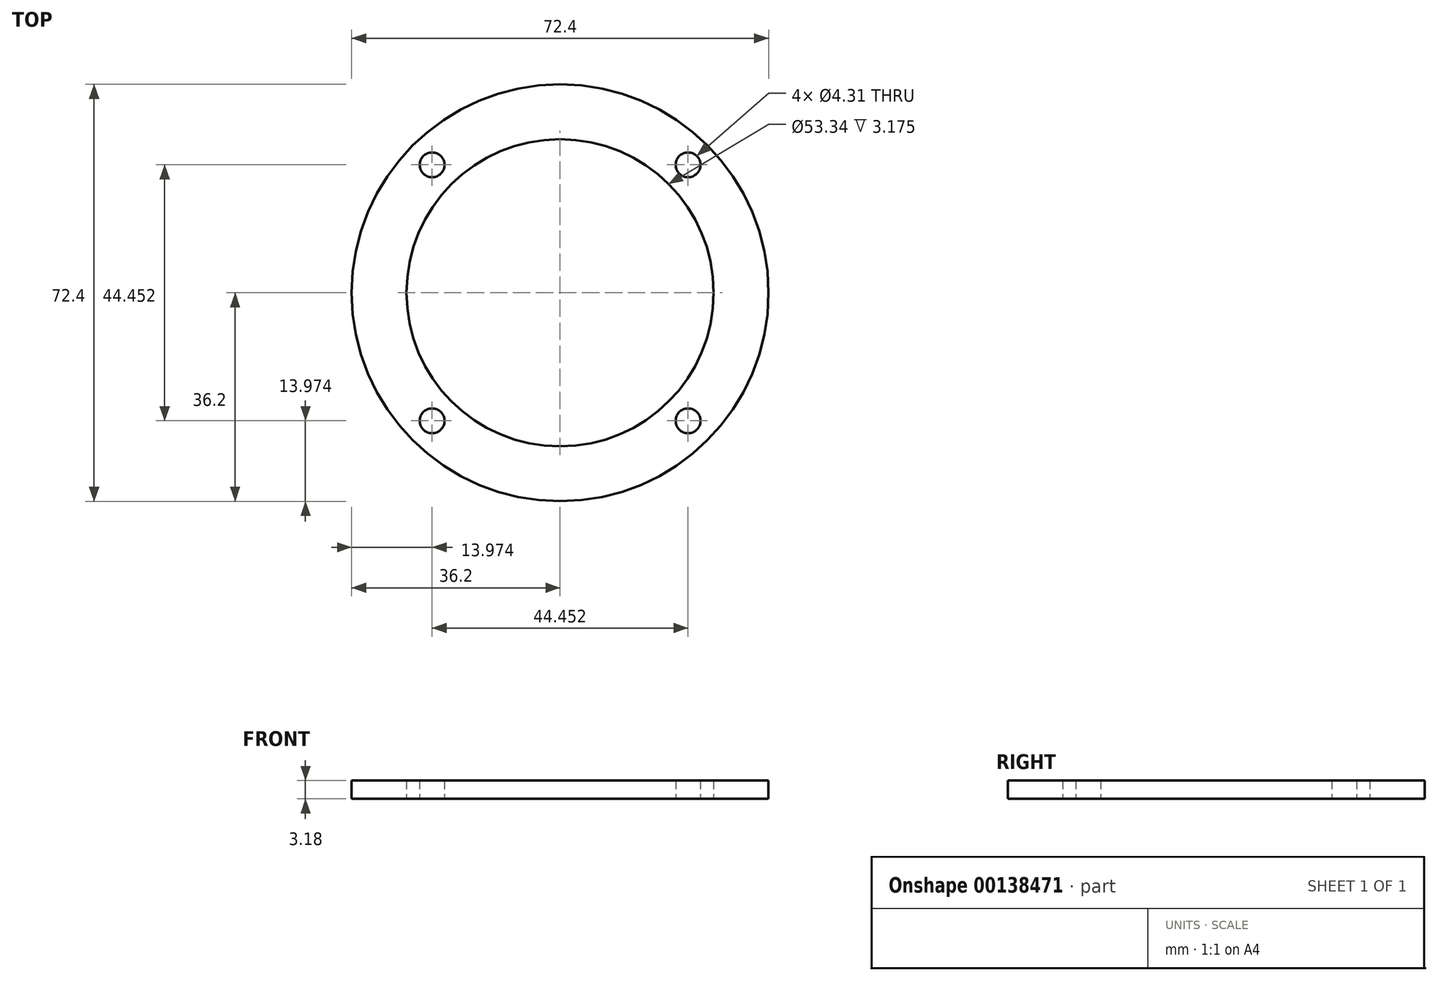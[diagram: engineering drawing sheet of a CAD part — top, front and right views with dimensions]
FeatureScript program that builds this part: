
annotation { "Feature Type Name" : "Feature", "Feature Type Description" : "" }
export const myFeature = defineFeature(function(context is Context, id is Id, definition is map)
    precondition{}
    {
        {
            var Q0;
            Q0=qCreatedBy(makeId("Top.planeOp"),FACE);
            var sketch = newSketch(context, id + "F0", { "sketchPlane" : qUnion([Q0])});
            skCircle(sketch, "E0", {"center": v(0, 0) * mm, "radius": 26.67 * mm});
            skLineSegment(sketch, "E1.bottom", {"start": v(22.23, 22.23) * mm, "end": v(-22.23, 22.23) * mm, "construction": true});
            skLineSegment(sketch, "E1.top", {"start": v(22.23, -22.23) * mm, "end": v(-22.23, -22.23) * mm, "construction": true});
            skLineSegment(sketch, "E1.left", {"start": v(22.23, 22.23) * mm, "end": v(22.23, -22.23) * mm, "construction": true});
            skLineSegment(sketch, "E1.right", {"start": v(-22.23, 22.23) * mm, "end": v(-22.23, -22.23) * mm, "construction": true});
            skCircle(sketch, "E2", {"center": v(-22.23, 22.23) * mm, "radius": 4.76 * mm, "construction": true});
            skCircle(sketch, "E3", {"center": v(-22.23, 22.23) * mm, "radius": 2.15 * mm});
            skCircle(sketch, "E4", {"center": v(22.23, 22.23) * mm, "radius": 2.15 * mm});
            skCircle(sketch, "E5", {"center": v(22.23, -22.23) * mm, "radius": 2.15 * mm});
            skCircle(sketch, "E6", {"center": v(-22.23, -22.23) * mm, "radius": 2.15 * mm});
            skCircle(sketch, "E7", {"center": v(0, 0) * mm, "radius": 36.2 * mm});
            skSolve(sketch);
        }
        {
            var Q0;
            Q0=qSketchRegion(id+"F0",true);
            extrude(context, id + "F1", {"entities" : qUnion([Q0]), "depth" : 3.17 * mm});
        }
    });
